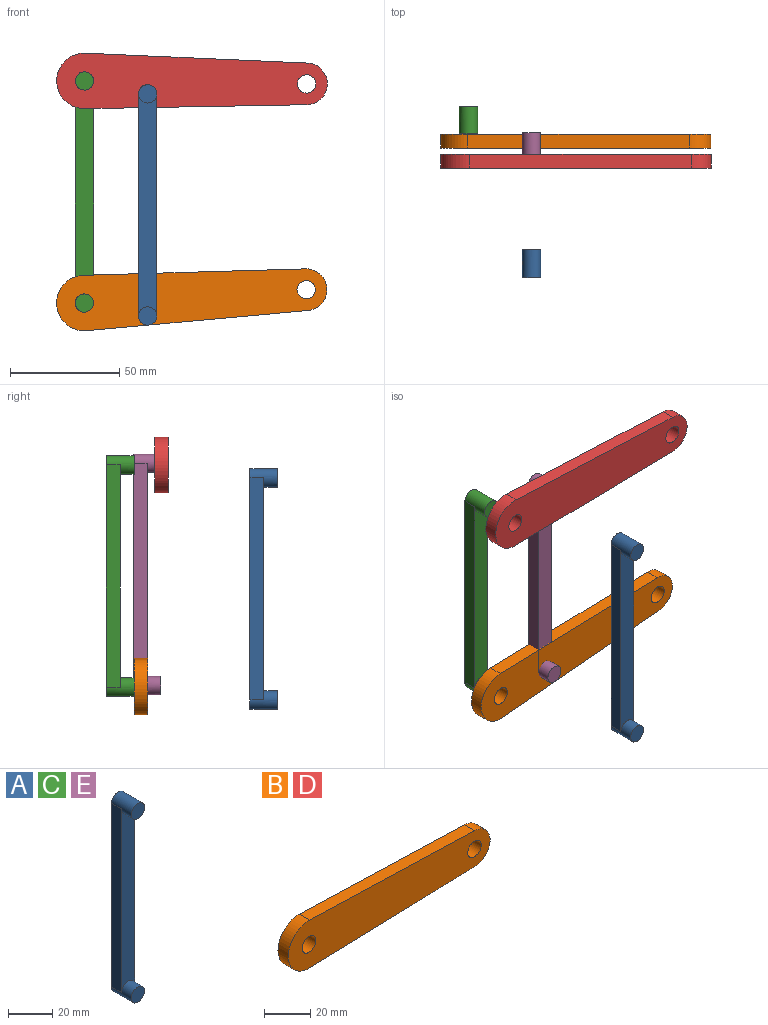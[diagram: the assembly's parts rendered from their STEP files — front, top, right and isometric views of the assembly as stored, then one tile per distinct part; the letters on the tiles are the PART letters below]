
ASSEMBLY  parts=5 mates=2
PART A: 8 faces, bbox 8.4x12.7x110 mm
  f0: plane 101.6x8.38mm, normal (0,-1,0), area 796.4mm2, adj f1,f2,f3,f4
  f1: cylinder r=4.19mm len=12.7mm, axis (0,1,0), area 250.8mm2, adj f0,f2,f4,f5,f6
  f2: plane 101.6x6.35mm, normal (1,0,0), area 645.2mm2, adj f0,f1,f3,f5
  f3: cylinder r=4.19mm len=12.7mm, axis (0,1,0), area 250.8mm2, adj f0,f2,f4,f5,f7
  f4: plane 101.6x6.35mm, normal (-1,0,0), area 645.2mm2, adj f0,f1,f3,f5
  f5: plane 109.98x8.38mm, normal (0,1,0), area 906.8mm2, adj f1,f2,f3,f4
  f6: plane 8.38x8.38mm, normal (0,-1,0), area 55.2mm2, adj f1
  f7: plane 8.38x8.38mm, normal (0,-1,0), area 55.2mm2, adj f3
PART B: 8 faces, bbox 123.8x6.4x25.4 mm
  f0: plane 101.5x6.35mm, normal (0.03,0,1), area 644.8mm2, adj f1,f4,f6,f7
  f1: cylinder r=12.7mm len=25.4mm, axis (0,1,0), area 258.4mm2, adj f0,f2,f6,f7
  f2: plane 101.5x6.35mm, normal (0.03,0,-1), area 644.8mm2, adj f1,f4,f6,f7
  f3: cylinder r=4.19mm len=8.38mm, axis (0,1,0), area 167.2mm2, adj f6,f7
  f4: cylinder r=9.53mm len=19.04mm, axis (0,1,0), area 186.2mm2, adj f0,f2,f6,f7
  f5: cylinder r=4.19mm len=8.38mm, axis (0,1,0), area 167.2mm2, adj f6,f7
  f6: plane 123.83x25.4mm, normal (0,-1,0), area 2544.7mm2, adj f0,f1,f2,f3,f4,f5
  f7: plane 123.83x25.4mm, normal (0,1,0), area 2544.7mm2, adj f0,f1,f2,f3,f4,f5
PART C: same geometry as A
PART D: same geometry as B
PART E: same geometry as A
PLACE A t=(0.15,-53.38,-6.61)mm
PLACE B rot(axis=(0,-1,0),3.5deg) t=(-24.54,-0.42,7.41)mm
PLACE C t=(-28.73,12.28,-0.7)mm
PLACE D rot(axis=(0,1,0),0.8deg) t=(-24.54,-9.77,109.01)mm
PLACE E at identity
MATE cylindrical C.f1 <-> B.f1  axis (0,-1,0) through (-24.54,-0.42,7.41)mm
MATE cylindrical C.f3 <-> D.f1  axis (0,-1,0) through (-24.54,-0.42,109.01)mm
